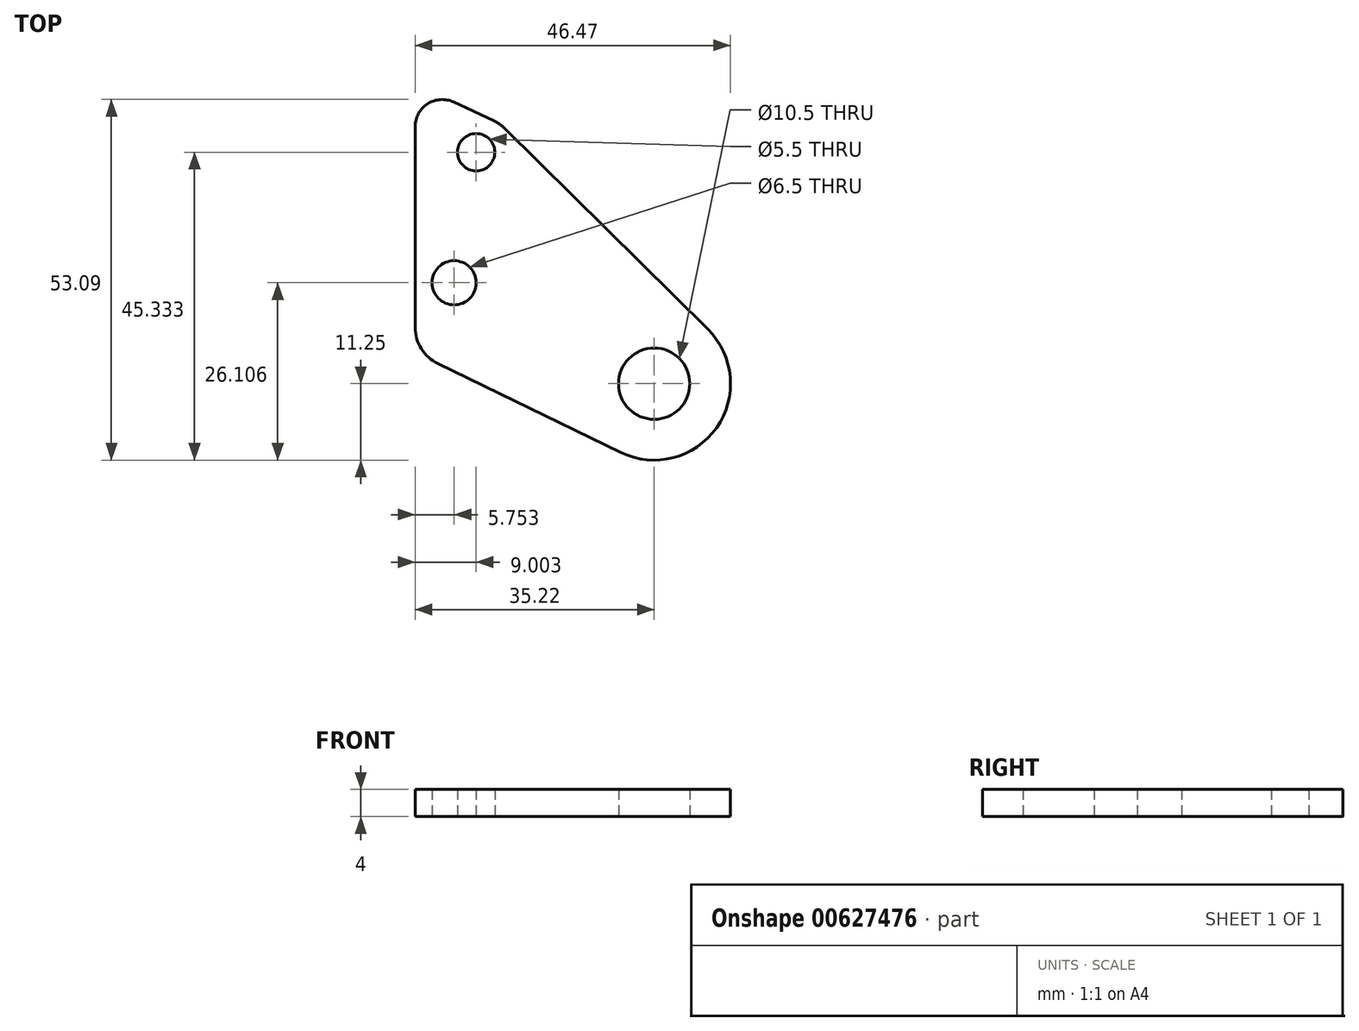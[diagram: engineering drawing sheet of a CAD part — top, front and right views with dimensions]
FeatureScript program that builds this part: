
annotation { "Feature Type Name" : "Feature", "Feature Type Description" : "" }
export const myFeature = defineFeature(function(context is Context, id is Id, definition is map)
    precondition{}
    {
        {
            var Q0;
            Q0=qCreatedBy(makeId("Top.planeOp"),FACE);
            var sketch = newSketch(context, id + "F0", { "sketchPlane" : qUnion([Q0])});
            skCircle(sketch, "E0", {"center": v(0, 0) * mm, "radius": 5.25 * mm});
            skArc(sketch, "E1", {"start": v(-4.9, -10.12) * mm, "mid": v(9.19, -6.5) * mm, "end": v(7.9, 8) * mm});
            skLineSegment(sketch, "E2", {"start": v(7.9, 8) * mm, "end": v(-22.75, 38.3) * mm});
            skLineSegment(sketch, "E3", {"start": v(-22.75, 38.3) * mm, "end": v(-35.22, 44.12) * mm});
            skLineSegment(sketch, "E4", {"start": v(-35.22, 44.12) * mm, "end": v(-35.22, 4.57) * mm});
            skLineSegment(sketch, "E5", {"start": v(-35.22, 4.57) * mm, "end": v(-4.9, -10.12) * mm});
            skCircle(sketch, "E6", {"center": v(-26.22, 34.08) * mm, "radius": 2.75 * mm});
            skCircle(sketch, "E7", {"center": v(-29.47, 14.86) * mm, "radius": 3.25 * mm});
            skSolve(sketch);
        }
        {
            var Q0;
            Q0=makeQuery(id+"F0.imprint","IMPRINT",FACE,{"disambiguationData":[TD([[makeQuery(id+"F0.imprint","IMPRINT",EDGE,{"derivedFrom":sQuery(id+"F0.wireOp",EDGE,"E0")}),-1.0]])]});
            extrude(context, id + "F1", {"entities" : qUnion([Q0]), "depth" : 4 * mm, "offsetDistance" : 25 * mm});
        }
        {
            var Q0;
            Q0=makeQuery(id+"F1.opExtrude","SWEPT_EDGE",EDGE,{"disambiguationData":[OSD([sQuery(id+"F0.wireOp",EDGE,"E2"),sQuery(id+"F0.wireOp",EDGE,"E3")])]});
            var Q1;
            Q1=makeQuery(id+"F1.opExtrude","SWEPT_EDGE",EDGE,{"disambiguationData":[OSD([sQuery(id+"F0.wireOp",EDGE,"E4"),sQuery(id+"F0.wireOp",EDGE,"E5")])]});
            fillet(context, id + "F2", {"entities" : qUnion([Q0, Q1]), "radius" : 6 * mm, "tangentPropagation" : true, "allowEdgeOverflow" : false});
        }
        {
            var Q0;
            Q0=makeQuery(id+"F1.opExtrude","SWEPT_EDGE",EDGE,{"disambiguationData":[OSD([sQuery(id+"F0.wireOp",EDGE,"E3"),sQuery(id+"F0.wireOp",EDGE,"E4")])]});
            fillet(context, id + "F3", {"entities" : qUnion([Q0]), "radius" : 4 * mm, "tangentPropagation" : true, "allowEdgeOverflow" : false});
        }
    });
